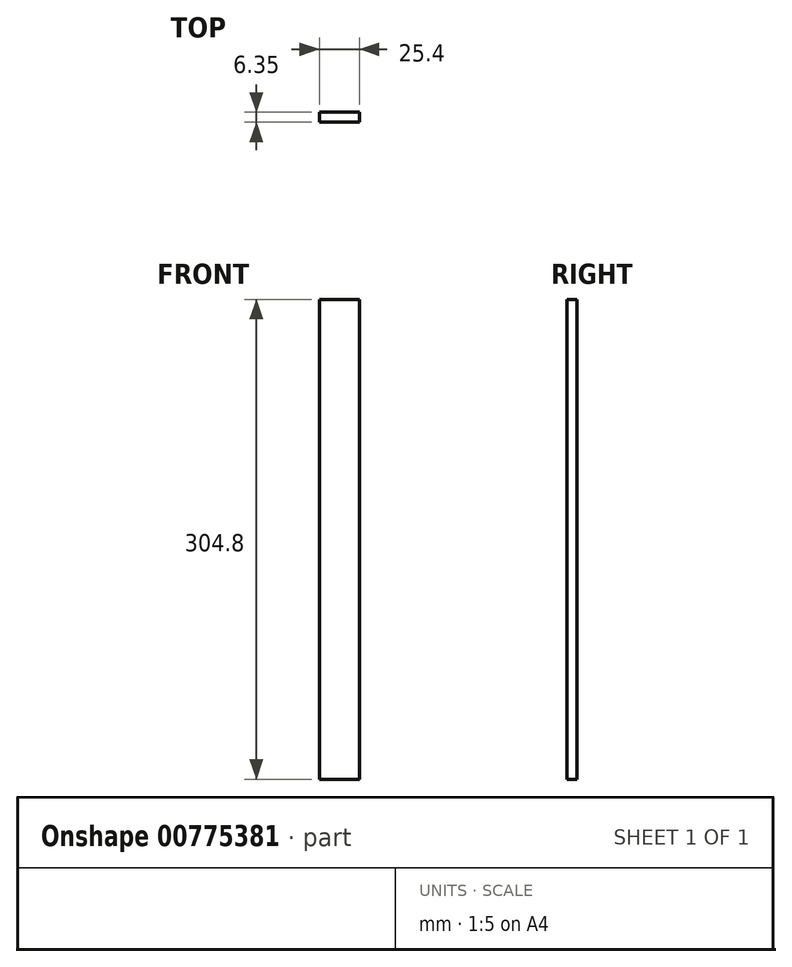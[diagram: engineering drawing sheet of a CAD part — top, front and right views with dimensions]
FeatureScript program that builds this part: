
annotation { "Feature Type Name" : "Feature", "Feature Type Description" : "" }
export const myFeature = defineFeature(function(context is Context, id is Id, definition is map)
    precondition{}
    {
        {
            var Q0;
            Q0=qCreatedBy(makeId("Front.planeOp"),FACE);
            var sketch = newSketch(context, id + "F0", { "sketchPlane" : qUnion([Q0])});
            skLineSegment(sketch, "E0.bottom", {"start": v(-12.7, 152.4) * mm, "end": v(12.7, 152.4) * mm});
            skLineSegment(sketch, "E0.top", {"start": v(-12.7, -152.4) * mm, "end": v(12.7, -152.4) * mm});
            skLineSegment(sketch, "E0.left", {"start": v(-12.7, 152.4) * mm, "end": v(-12.7, -152.4) * mm});
            skLineSegment(sketch, "E0.right", {"start": v(12.7, 152.4) * mm, "end": v(12.7, -152.4) * mm});
            skPoint(sketch, "E0.middle", {"position": v(0, 0) * mm});
            skSolve(sketch);
        }
        {
            var Q0;
            Q0=makeQuery(id+"F0.imprint","IMPRINT",FACE,{"disambiguationData":[TD([[makeQuery(id+"F0.imprint","IMPRINT",EDGE,{"derivedFrom":sQuery(id+"F0.wireOp",EDGE,"E0.bottom")}),-1.0]])]});
            extrude(context, id + "F1", {"entities" : qUnion([Q0]), "depth" : 6.35 * mm, "offsetDistance" : 25.4 * mm});
        }
    });
